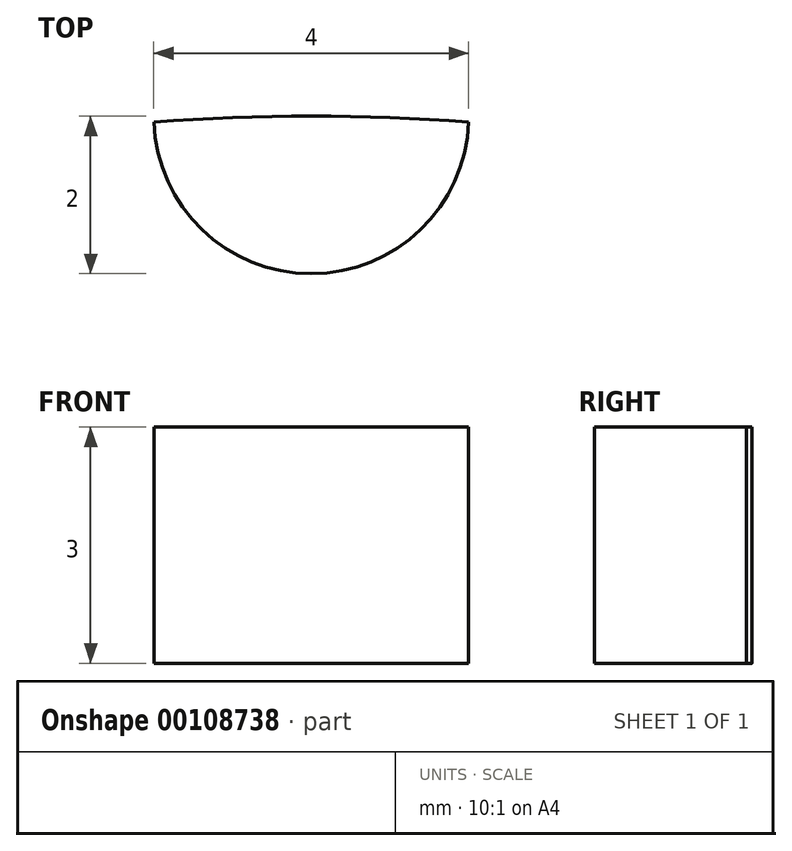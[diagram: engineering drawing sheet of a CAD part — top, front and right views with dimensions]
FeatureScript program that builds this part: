
annotation { "Feature Type Name" : "Feature", "Feature Type Description" : "" }
export const myFeature = defineFeature(function(context is Context, id is Id, definition is map)
    precondition{}
    {
        {
            var Q0;
            Q0=qCreatedBy(makeId("Top.planeOp"),FACE);
            var sketch = newSketch(context, id + "F0", { "sketchPlane" : qUnion([Q0])});
            skCircle(sketch, "E0", {"center": v(0, 0) * mm, "radius": 27 * mm});
            skLineSegment(sketch, "E1", {"start": v(0, 27) * mm, "end": v(0, -27) * mm, "construction": true});
            skCircle(sketch, "E2", {"center": v(0, 9.5) * mm, "radius": 3.12 * mm});
            skCircle(sketch, "E3", {"center": v(0, -9.5) * mm, "radius": 3.12 * mm});
            skLineSegment(sketch, "E4", {"start": v(0, -12.62) * mm, "end": v(-23.87, -12.62) * mm});
            skLineSegment(sketch, "E5", {"start": v(0, 6.37) * mm, "end": v(26.24, 6.37) * mm});
            skLineSegment(sketch, "E6", {"start": v(0, 9.5) * mm, "end": v(25.27, 9.5) * mm});
            skLineSegment(sketch, "E7", {"start": v(0, -9.5) * mm, "end": v(-25.27, -9.5) * mm});
            skLineSegment(sketch, "E8", {"start": v(-27, 0) * mm, "end": v(27, 0) * mm, "construction": true});
            skSolve(sketch);
        }
        {
            var Q0;
            {var subQ0=sQuery(id+"F0.wireOp",EDGE,"E4");Q0=makeQuery(id+"F0.imprint","IMPRINT",FACE,{"disambiguationData":[TD([[makeQuery(id+"F0.imprint","IMPRINT",EDGE,{"derivedFrom":subQ0}),1.0]])]});}
            extrude(context, id + "F1", {"entities" : qUnion([Q0]), "depth" : 3 * mm});
        }
        {
            var Q0;
            Q0=makeQuery(id+"F1.opExtrude","SWEPT_EDGE",EDGE,{"disambiguationData":[OSD([sQuery(id+"F0.wireOp",EDGE,"E0"),sQuery(id+"F0.wireOp",EDGE,"E7")])]});
            var Q1;
            Q1=makeQuery(id+"F1.opExtrude","SWEPT_EDGE",EDGE,{"disambiguationData":[OSD([sQuery(id+"F0.wireOp",EDGE,"E0"),sQuery(id+"F0.wireOp",EDGE,"E5")])]});
            fillet(context, id + "F2", {"entities" : qUnion([Q0, Q1]), "radius" : 3 * mm, "tangentPropagation" : true, "allowEdgeOverflow" : false});
        }
        {
            var Q0;
            Q0=makeQuery(id+"F1.opExtrude","SWEPT_EDGE",EDGE,{"disambiguationData":[OSD([sQuery(id+"F0.wireOp",EDGE,"E0"),sQuery(id+"F0.wireOp",EDGE,"E6")])]});
            var Q1;
            Q1=makeQuery(id+"F1.opExtrude","SWEPT_EDGE",EDGE,{"disambiguationData":[OSD([sQuery(id+"F0.wireOp",EDGE,"E0"),sQuery(id+"F0.wireOp",EDGE,"E4")])]});
            fillet(context, id + "F3", {"entities" : qUnion([Q0, Q1]), "radius" : 1 * mm, "tangentPropagation" : true, "allowEdgeOverflow" : false});
        }
        {
            var Q0;
            Q0=makeQuery(id+"F1.opExtrude","CAP_FACE",FACE,{"disambiguationData":[OSD([sQuery(id+"F0.wireOp",EDGE,"E0"),sQuery(id+"F0.wireOp",EDGE,"E2"),sQuery(id+"F0.wireOp",EDGE,"E3"),sQuery(id+"F0.wireOp",EDGE,"E4"),sQuery(id+"F0.wireOp",EDGE,"E5"),sQuery(id+"F0.wireOp",EDGE,"E6"),sQuery(id+"F0.wireOp",EDGE,"E7")])],"isStart":false});
            var sketch = newSketch(context, id + "F4", { "sketchPlane" : qUnion([Q0])});
            skArc(sketch, "E9", {"start": v(2, -26.93) * mm, "mid": v(0, -25) * mm, "end": v(-2, -26.93) * mm});
            skCircle(sketch, "E10.0", {"center": v(0, 0) * mm, "radius": 27 * mm});
            skArc(sketch, "E11.MirrorCS", {"start": v(2, 26.93) * mm, "mid": v(0, 25) * mm, "end": v(-2, 26.93) * mm});
            skSolve(sketch);
        }
        {
            var Q0;
            {var subQ0=sQuery(id+"F4.wireOp",EDGE,"E11.MirrorCS");Q0=makeQuery(id+"F4.imprint","IMPRINT",FACE,{"disambiguationData":[TD([[makeQuery(id+"F4.imprint","IMPRINT",EDGE,{"derivedFrom":subQ0}),-1.0]])]});}
            var Q1;
            {var subQ0=sQuery(id+"F4.wireOp",EDGE,"E9");Q1=makeQuery(id+"F4.imprint","IMPRINT",FACE,{"disambiguationData":[TD([[makeQuery(id+"F4.imprint","IMPRINT",EDGE,{"derivedFrom":subQ0}),1.0]])]});}
            extrude(context, id + "F5", {"entities" : qUnion([Q0, Q1]), "operationType" : NewBodyOperationType.REMOVE, "oppositeDirection" : true, "depth" : 25 * mm});
        }
    });
